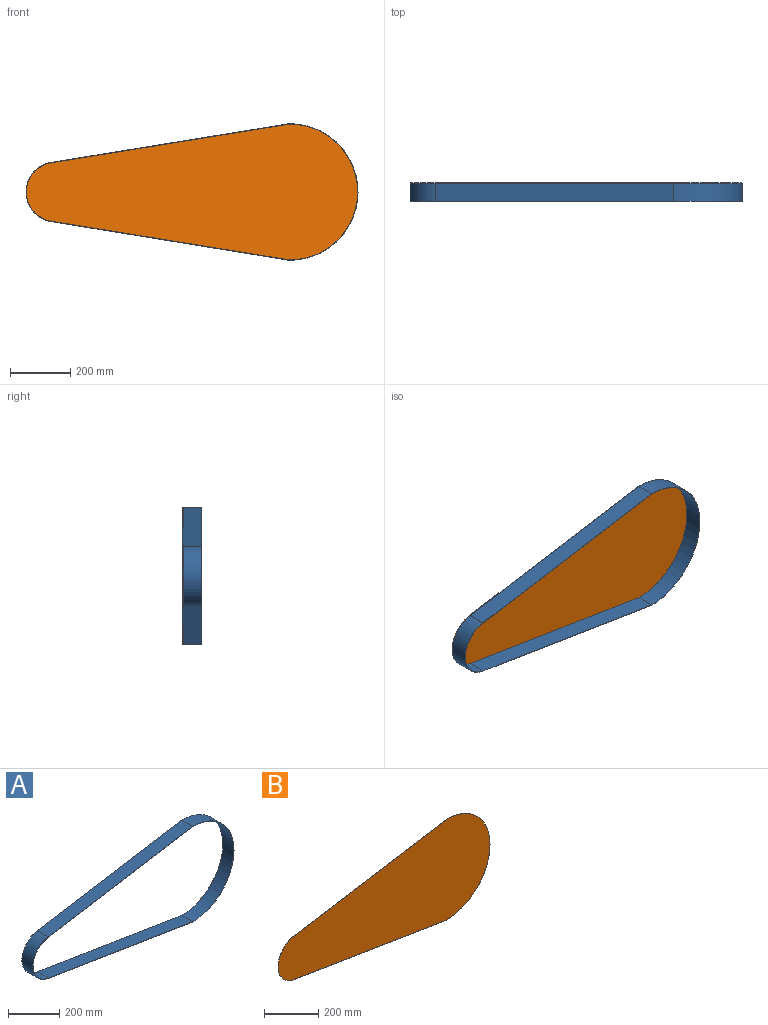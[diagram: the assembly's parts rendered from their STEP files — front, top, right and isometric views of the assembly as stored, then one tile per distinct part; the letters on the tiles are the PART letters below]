
ASSEMBLY  parts=2 mates=1
PART A: 10 faces, bbox 1105x60x455 mm
  f0: plane 793.52x128.79mm, normal (-0.16,0,-0.99), area 48234.3mm2, adj f1,f7,f8,f9
  f1: cylinder r=227.5mm len=455mm, axis (0,1,0), area 42882.7mm2, adj f0,f2,f8,f9
  f2: plane 793.52x128.79mm, normal (-0.16,0,0.99), area 48234.3mm2, adj f1,f7,f8,f9
  f3: cylinder r=98.5mm len=194.46mm, axis (0,1,0), area 16665mm2, adj f4,f6,f8,f9
  f4: plane 793.4x128.77mm, normal (0.16,0,-0.99), area 48227mm2, adj f3,f5,f8,f9
  f5: cylinder r=226mm len=452mm, axis (0,1,0), area 42585.5mm2, adj f4,f6,f8,f9
  f6: plane 793.4x128.77mm, normal (0.16,0,0.99), area 48227mm2, adj f3,f5,f8,f9
  f7: cylinder r=100mm len=197.42mm, axis (0,1,0), area 16918.7mm2, adj f0,f2,f8,f9
  f8: plane 1105x455mm, normal (0,-1,0), area 3899.7mm2, adj f0,f1,f2,f3,f4,f5,f6,f7
  f9: plane 1105x455mm, normal (0,1,0), area 3899.7mm2, adj f0,f1,f2,f3,f4,f5,f6,f7
PART B: 6 faces, bbox 1105x1.5x455 mm
  f0: plane 793.52x128.79mm, normal (-0.16,0,-0.99), area 1205.9mm2, adj f1,f3,f4,f5
  f1: cylinder r=227.5mm len=455mm, axis (0,1,0), area 1072.1mm2, adj f0,f2,f4,f5
  f2: plane 793.52x128.79mm, normal (-0.16,0,0.99), area 1205.9mm2, adj f1,f3,f4,f5
  f3: cylinder r=100mm len=197.42mm, axis (0,1,0), area 423mm2, adj f0,f2,f4,f5
  f4: plane 1105x455mm, normal (0,-1,0), area 352669.2mm2, adj f0,f1,f2,f3
  f5: plane 1105x455mm, normal (0,1,0), area 352669.2mm2, adj f0,f1,f2,f3
PLACE A t=(43.02,-118.37,21.65)mm
PLACE B t=(43.02,-117.62,21.65)mm
MATE fastened B.f4 <-> A.f9  axis (0,-1,0) through (43.02,-118.37,249.15)mm
